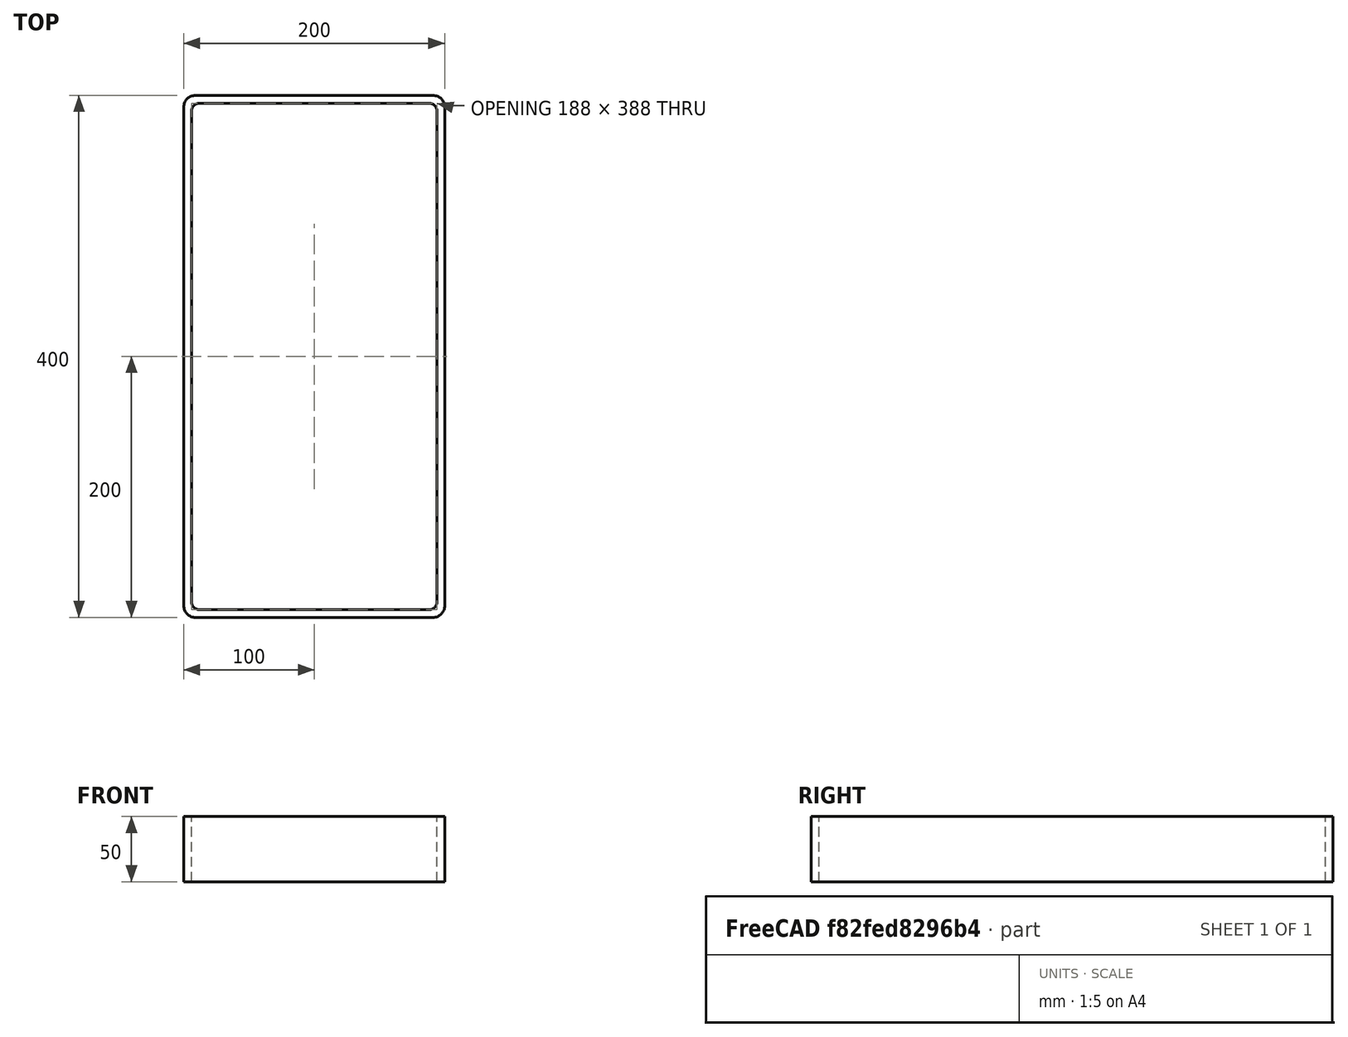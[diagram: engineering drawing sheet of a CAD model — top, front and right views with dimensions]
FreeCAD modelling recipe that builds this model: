
FCSTD DOCUMENT  (FreeCAD 0.15R4671 (Git))
Label: Rectangular hollow section 400x200x6 EN10219 S235JRH
License: All rights reserved
LicenseURL: http://en.wikipedia.org/wiki/All_rights_reserved
objects: Sketcher::SketchObject×1, Part::Extrusion×1
note: 2 computed .brp shape members not serialized (recipe doc carries the construction recipe); baked Part::Feature solids carry a one-line shape summary decoded from their .brp

FEATURE [Sketcher::SketchObject] Sketch
  sketch-geometry (16):
    g0: LineSegment StartX=-88 StartY=194 StartZ=0 EndX=88 EndY=194 EndZ=0
    g1: LineSegment StartX=94 StartY=188 StartZ=0 EndX=94 EndY=-188 EndZ=0
    g2: LineSegment StartX=88 StartY=-194 StartZ=0 EndX=-88 EndY=-194 EndZ=0
    g3: LineSegment StartX=-94 StartY=-188 StartZ=0 EndX=-94 EndY=188 EndZ=0
    g4: LineSegment StartX=-91 StartY=200 StartZ=0 EndX=91 EndY=200 EndZ=0
    g5: LineSegment StartX=100 StartY=191 StartZ=0 EndX=100 EndY=-191 EndZ=0
    g6: LineSegment StartX=91 StartY=-200 StartZ=0 EndX=-91 EndY=-200 EndZ=0
    g7: LineSegment StartX=-100 StartY=-191 StartZ=0 EndX=-100 EndY=191 EndZ=0
    g8: ArcOfCircle CenterX=-88 CenterY=188 CenterZ=0 NormalX=0 NormalY=0 NormalZ=1 Radius=6 StartAngle=1.5708 EndAngle=3.14159
    g9: ArcOfCircle CenterX=88 CenterY=188 CenterZ=0 NormalX=0 NormalY=0 NormalZ=1 Radius=6 StartAngle=0 EndAngle=1.5708
    g10: ArcOfCircle CenterX=88 CenterY=-188 CenterZ=0 NormalX=0 NormalY=0 NormalZ=1 Radius=6 StartAngle=4.71239 EndAngle=6.28319
    g11: ArcOfCircle CenterX=-88 CenterY=-188 CenterZ=0 NormalX=0 NormalY=0 NormalZ=1 Radius=6 StartAngle=3.14159 EndAngle=4.71239
    g12: ArcOfCircle CenterX=91 CenterY=191 CenterZ=0 NormalX=0 NormalY=0 NormalZ=1 Radius=9 StartAngle=0 EndAngle=1.5708
    g13: ArcOfCircle CenterX=91 CenterY=-191 CenterZ=0 NormalX=0 NormalY=0 NormalZ=1 Radius=9 StartAngle=4.71239 EndAngle=6.28319
    g14: ArcOfCircle CenterX=-91 CenterY=-191 CenterZ=0 NormalX=0 NormalY=0 NormalZ=1 Radius=9 StartAngle=3.14159 EndAngle=4.71239
    g15: ArcOfCircle CenterX=-91 CenterY=191 CenterZ=0 NormalX=0 NormalY=0 NormalZ=1 Radius=9 StartAngle=1.5708 EndAngle=3.14159
  constraints (36):
    c: Horizontal(g2)
    c: Vertical(g3)
    c: Horizontal(g6)
    c: Vertical(g7)
    c: Tangent(g3,g8) = 1.5708
    c: Tangent(g0,g8) = 1.5708
    c: Tangent(g0,g9) = 1.5708
    c: Tangent(g1,g9) = 1.5708
    c: Tangent(g1,g10) = 1.5708
    c: Tangent(g2,g10) = 1.5708
    c: Tangent(g2,g11) = 1.5708
    c: Tangent(g3,g11) = 1.5708
    c: Tangent(g4,g12) = 1.5708
    c: Tangent(g5,g12) = 1.5708
    c: Tangent(g5,g13) = 1.5708
    c: Tangent(g6,g13) = 1.5708
    c: Tangent(g6,g14) = 1.5708
    c: Tangent(g7,g14) = 1.5708
    c: Tangent(g7,g15) = 1.5708
    c: Tangent(g4,g15) = 1.5708
    c: Equal(g9,g8)
    c: Equal(g9,g11)
    c: Equal(g9,g10)
    c: Equal(g12,g15)
    c: Equal(g12,g14)
    c: Equal(g12,g13)
    c: Symmetric(g4,g6,g-1)
    c: Symmetric(g7,g5,g-2)
    c: DistanceY(g4,g6) = -400
    c: DistanceX(g7,g5) = 200
    c: Symmetric(g3,g1,g-2)
    c: Symmetric(g0,g2,g-1)
    c: DistanceY(g0,g4) = 6
    c: DistanceX(g5,g1) = -6
    c: Radius(g9) = 6
    c: Radius(g12) = 9
FEATURE [Part::Extrusion] Extrude  label="Rectangular hollow section 400x200x6 EN10219 S235JRH"
  Base = -> Sketch
  Dir = (0,0,50)
  Solid = true
